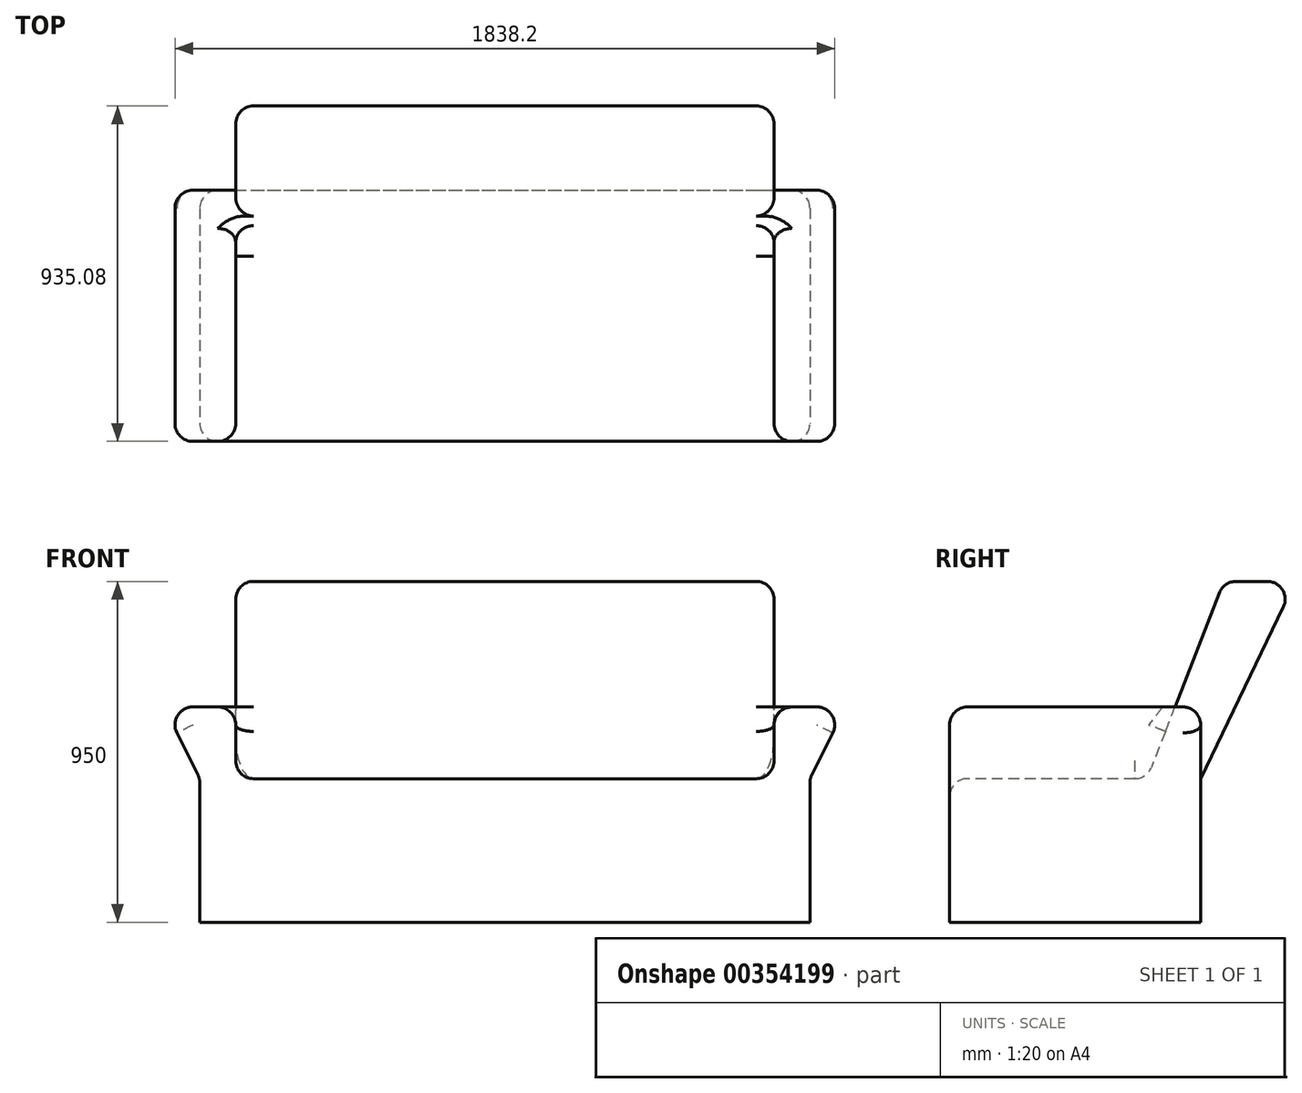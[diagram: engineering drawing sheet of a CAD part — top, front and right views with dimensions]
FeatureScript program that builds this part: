
annotation { "Feature Type Name" : "Feature", "Feature Type Description" : "" }
export const myFeature = defineFeature(function(context is Context, id is Id, definition is map)
    precondition{}
    {
        {
            var Q0;
            Q0=qCreatedBy(makeId("Front.planeOp"),FACE);
            var sketch = newSketch(context, id + "F0", { "sketchPlane" : qUnion([Q0])});
            skLineSegment(sketch, "E0.bottom", {"start": v(-850, 0) * mm, "end": v(850, 0) * mm});
            skLineSegment(sketch, "E0.top", {"start": v(-850, 400) * mm, "end": v(850, 400) * mm});
            skLineSegment(sketch, "E0.left", {"start": v(-850, 0) * mm, "end": v(-850, 400) * mm});
            skLineSegment(sketch, "E0.right", {"start": v(850, 0) * mm, "end": v(850, 400) * mm});
            skLineSegment(sketch, "E1", {"start": v(-750, 400) * mm, "end": v(-750, 600) * mm});
            skLineSegment(sketch, "E2", {"start": v(-750, 600) * mm, "end": v(-950, 600) * mm});
            skLineSegment(sketch, "E3", {"start": v(-950, 600) * mm, "end": v(-850, 400) * mm});
            skLineSegment(sketch, "E4", {"start": v(750, 400) * mm, "end": v(750, 600) * mm});
            skLineSegment(sketch, "E5", {"start": v(750, 600) * mm, "end": v(950, 600) * mm});
            skLineSegment(sketch, "E6", {"start": v(950, 600) * mm, "end": v(850, 400) * mm});
            skSolve(sketch);
        }
        {
            var Q0;
            Q0=qSketchRegion(id+"F0",true);
            extrude(context, id + "F1", {"entities" : qUnion([Q0]), "oppositeDirection" : true, "depth" : 700 * mm});
        }
        {
            var Q0;
            Q0=qCreatedBy(makeId("Right.planeOp"),FACE);
            var sketch = newSketch(context, id + "F2", { "sketchPlane" : qUnion([Q0])});
            skLineSegment(sketch, "E7", {"start": v(700, 400) * mm, "end": v(964.63, 950) * mm});
            skLineSegment(sketch, "E8", {"start": v(964.63, 950) * mm, "end": v(764.63, 950) * mm});
            skLineSegment(sketch, "E9", {"start": v(764.63, 950) * mm, "end": v(550, 400) * mm});
            skLineSegment(sketch, "E10", {"start": v(550, 400) * mm, "end": v(700, 400) * mm});
            skSolve(sketch);
        }
        {
            var Q0;
            Q0=makeQuery(id+"F2.imprint","IMPRINT",FACE,{"disambiguationData":[TD([[makeQuery(id+"F2.imprint","IMPRINT",EDGE,{"derivedFrom":sQuery(id+"F2.wireOp",EDGE,"E7")}),1.0]])]});
            extrude(context, id + "F3", {"entities" : qUnion([Q0]), "operationType" : NewBodyOperationType.ADD, "endBound" : BoundingType.SYMMETRIC, "oppositeDirection" : true, "depth" : 1500 * mm});
        }
        {
            var Q0;
            Q0=makeQuery(id+"F1.opExtrude","SWEPT_EDGE",EDGE,{"disambiguationData":[OSD([sQuery(id+"F0.wireOp",EDGE,"E5"),sQuery(id+"F0.wireOp",EDGE,"E6")])]});
            var Q1;
            Q1=makeQuery(id+"F1.opExtrude","SWEPT_EDGE",EDGE,{"disambiguationData":[OSD([sQuery(id+"F0.wireOp",EDGE,"E2"),sQuery(id+"F0.wireOp",EDGE,"E3")])]});
            var Q2;
            {var subQ0=sQuery(id+"F0.wireOp",EDGE,"E4");var subQ1=sQuery(id+"F0.wireOp",EDGE,"E5");Q2=makeQuery(id+"F3.boolean.opBoolean","SPLIT",EDGE,{"disambiguationData":[topologyDisambiguationEdgeConnected([makeQuery(id+"F1.opExtrude","SWEPT_FACE",FACE,{"disambiguationData":[OSD([subQ0])]})])],"derivedFrom":makeQuery(id+"F1.opExtrude","SWEPT_EDGE",EDGE,{"disambiguationData":[OSD([subQ0,subQ1])]})});}
            var Q3;
            Q3=makeQuery(id+"F3.opExtrude","SWEPT_EDGE",EDGE,{"disambiguationData":[OSD([sQuery(id+"F2.wireOp",EDGE,"E8"),sQuery(id+"F2.wireOp",EDGE,"E9")])]});
            var Q4;
            {var subQ0=sQuery(id+"F0.wireOp",EDGE,"E1");var subQ1=sQuery(id+"F0.wireOp",EDGE,"E2");Q4=makeQuery(id+"F3.boolean.opBoolean","SPLIT",EDGE,{"disambiguationData":[topologyDisambiguationEdgeConnected([makeQuery(id+"F1.opExtrude","SWEPT_FACE",FACE,{"disambiguationData":[OSD([subQ0])]})])],"derivedFrom":makeQuery(id+"F1.opExtrude","SWEPT_EDGE",EDGE,{"disambiguationData":[OSD([subQ0,subQ1])]})});}
            var Q5;
            Q5=makeQuery(id+"F1.opExtrude","CAP_EDGE",EDGE,{"disambiguationData":[OSD([sQuery(id+"F0.wireOp",EDGE,"E5")])],"isStart":false});
            var Q6;
            Q6=makeQuery(id+"F1.opExtrude","CAP_EDGE",EDGE,{"disambiguationData":[OSD([sQuery(id+"F0.wireOp",EDGE,"E2")])],"isStart":false});
            var Q7;
            Q7=makeQuery(id+"F3.opExtrude","SWEPT_EDGE",EDGE,{"disambiguationData":[OSD([sQuery(id+"F2.wireOp",EDGE,"E7"),sQuery(id+"F2.wireOp",EDGE,"E8")])]});
            fillet(context, id + "F4", {"entities" : qUnion([Q0, Q1, Q2, Q3, Q4, Q5, Q6, Q7]), "radius" : 50 * mm, "tangentPropagation" : true, "allowEdgeOverflow" : false});
        }
        {
            var Q0;
            Q0=makeQuery(id+"F1.opExtrude","SWEPT_EDGE",EDGE,{"disambiguationData":[OSD([sQuery(id+"F0.wireOp",EDGE,"E0.top"),sQuery(id+"F0.wireOp",EDGE,"E0.right"),sQuery(id+"F0.wireOp",EDGE,"E6")])]});
            var Q1;
            Q1=makeQuery(id+"F1.opExtrude","SWEPT_EDGE",EDGE,{"disambiguationData":[OSD([sQuery(id+"F0.wireOp",EDGE,"E0.top"),sQuery(id+"F0.wireOp",EDGE,"E0.left"),sQuery(id+"F0.wireOp",EDGE,"E3")])]});
            var Q2;
            Q2=makeQuery(id+"F1.opExtrude","SWEPT_EDGE",EDGE,{"disambiguationData":[OSD([sQuery(id+"F0.wireOp",EDGE,"E0.top"),sQuery(id+"F0.wireOp",EDGE,"E1")])]});
            var Q3;
            Q3=makeQuery(id+"F1.opExtrude","SWEPT_EDGE",EDGE,{"disambiguationData":[OSD([sQuery(id+"F0.wireOp",EDGE,"E0.top"),sQuery(id+"F0.wireOp",EDGE,"E4")])]});
            fillet(context, id + "F5", {"entities" : qUnion([Q0, Q1, Q2, Q3]), "radius" : 50 * mm, "tangentPropagation" : true, "allowEdgeOverflow" : false});
        }
        {
            var Q0;
            Q0=makeQuery(id+"F1.opExtrude","CAP_EDGE",EDGE,{"disambiguationData":[OSD([sQuery(id+"F0.wireOp",EDGE,"E0.right")])],"isStart":true});
            var Q1;
            {var subQ0=sQuery(id+"F0.wireOp",EDGE,"E1");var subQ1=sQuery(id+"F0.wireOp",EDGE,"E2");Q1=makeQuery(id+"F4.opFillet","BLEND_EDGE",EDGE,{"blendedFrom":[makeQuery(id+"F3.boolean.opBoolean","SPLIT",EDGE,{"disambiguationData":[topologyDisambiguationEdgeConnected([makeQuery(id+"F1.opExtrude","SWEPT_FACE",FACE,{"disambiguationData":[OSD([subQ0])]})])],"derivedFrom":makeQuery(id+"F1.opExtrude","SWEPT_EDGE",EDGE,{"disambiguationData":[OSD([subQ0,subQ1])]})}),makeQuery(id+"F3.opExtrude","SWEPT_FACE",FACE,{"disambiguationData":[OSD([sQuery(id+"F2.wireOp",EDGE,"E9")])]})],"blendedInto":[makeQuery(id+"F3.opExtrude","SWEPT_FACE",FACE,{"disambiguationData":[OSD([sQuery(id+"F2.wireOp",EDGE,"E9")])]})]});}
            fillet(context, id + "F6", {"entities" : qUnion([Q0, Q1]), "radius" : 50 * mm, "tangentPropagation" : true, "allowEdgeOverflow" : false});
        }
        {
            var Q0;
            {var subQ0=sQuery(id+"F2.wireOp",EDGE,"E9");Q0=makeQuery(id+"F3.boolean.opBoolean","SPLIT",EDGE,{"disambiguationData":[topologyDisambiguationEdgeConnected([makeQuery(id+"F3.opExtrude","CAP_FACE",FACE,{"disambiguationData":[OSD([sQuery(id+"F2.wireOp",EDGE,"E7"),sQuery(id+"F2.wireOp",EDGE,"E8"),subQ0,sQuery(id+"F2.wireOp",EDGE,"E10")])],"isStart":true})])],"derivedFrom":makeQuery(id+"F3.opExtrude","CAP_EDGE",EDGE,{"disambiguationData":[OSD([subQ0])],"isStart":true})});}
            var Q1;
            {var subQ0=sQuery(id+"F2.wireOp",EDGE,"E9");Q1=makeQuery(id+"F3.boolean.opBoolean","SPLIT",EDGE,{"disambiguationData":[topologyDisambiguationEdgeConnected([makeQuery(id+"F3.opExtrude","CAP_FACE",FACE,{"disambiguationData":[OSD([sQuery(id+"F2.wireOp",EDGE,"E7"),sQuery(id+"F2.wireOp",EDGE,"E8"),subQ0,sQuery(id+"F2.wireOp",EDGE,"E10")])],"isStart":false})])],"derivedFrom":makeQuery(id+"F3.opExtrude","CAP_EDGE",EDGE,{"disambiguationData":[OSD([subQ0])],"isStart":false})});}
            fillet(context, id + "F7", {"entities" : qUnion([Q0, Q1]), "radius" : 50 * mm, "tangentPropagation" : true, "allowEdgeOverflow" : false});
        }
        {
            var Q0;
            Q0=makeQuery(id+"F1.opExtrude","CAP_EDGE",EDGE,{"disambiguationData":[OSD([sQuery(id+"F0.wireOp",EDGE,"E0.right")])],"isStart":false});
            var Q1;
            Q1=makeQuery(id+"F1.opExtrude","CAP_EDGE",EDGE,{"disambiguationData":[OSD([sQuery(id+"F0.wireOp",EDGE,"E0.left")])],"isStart":false});
            fillet(context, id + "F8", {"entities" : qUnion([Q0, Q1]), "radius" : 50 * mm, "tangentPropagation" : true, "allowEdgeOverflow" : false});
        }
    });
